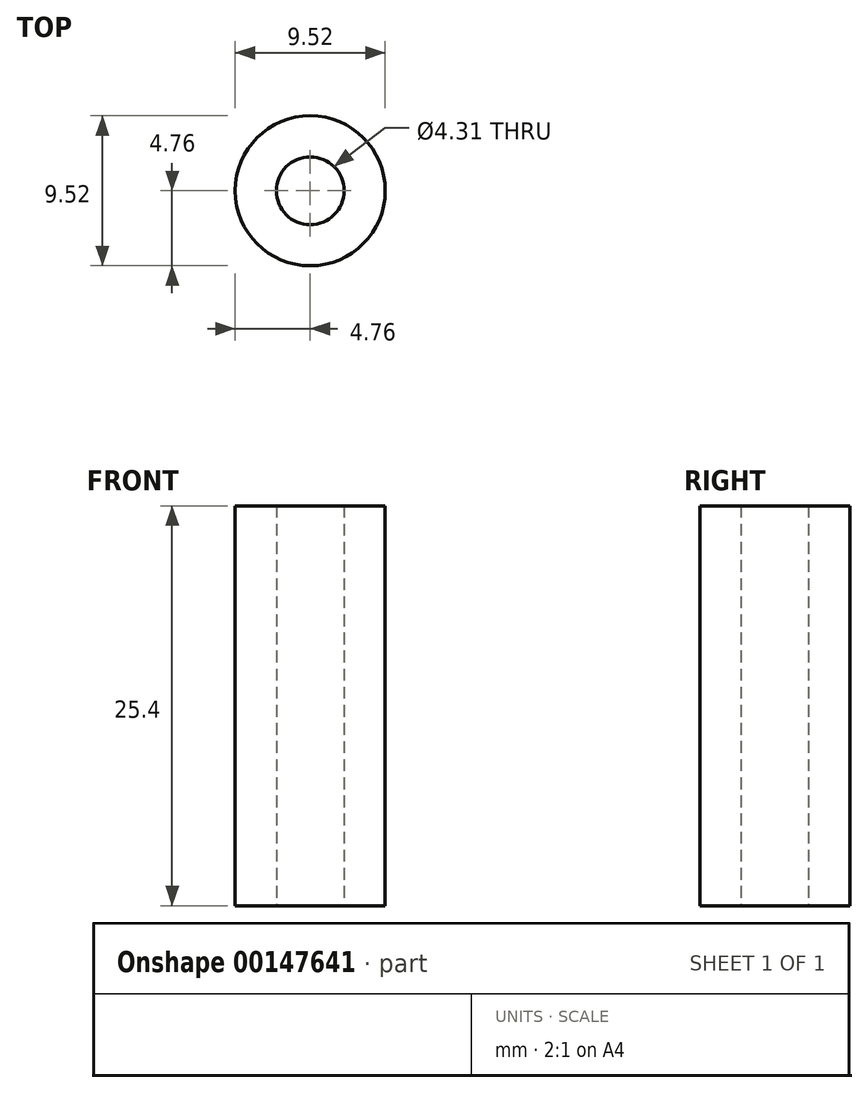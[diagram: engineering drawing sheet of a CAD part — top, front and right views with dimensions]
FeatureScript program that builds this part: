
annotation { "Feature Type Name" : "Feature", "Feature Type Description" : "" }
export const myFeature = defineFeature(function(context is Context, id is Id, definition is map)
    precondition{}
    {
        {
            var Q0;
            Q0=qCreatedBy(makeId("Top.planeOp"),FACE);
            var sketch = newSketch(context, id + "F0", { "sketchPlane" : qUnion([Q0])});
            skCircle(sketch, "E0", {"center": v(0, 0) * mm, "radius": 4.76 * mm});
            skCircle(sketch, "E1", {"center": v(0, 0) * mm, "radius": 2.15 * mm});
            skSolve(sketch);
        }
        {
            var Q0;
            Q0=qSketchRegion(id+"F0",true);
            extrude(context, id + "F1", {"entities" : qUnion([Q0]), "depth" : 25.4 * mm});
        }
    });
